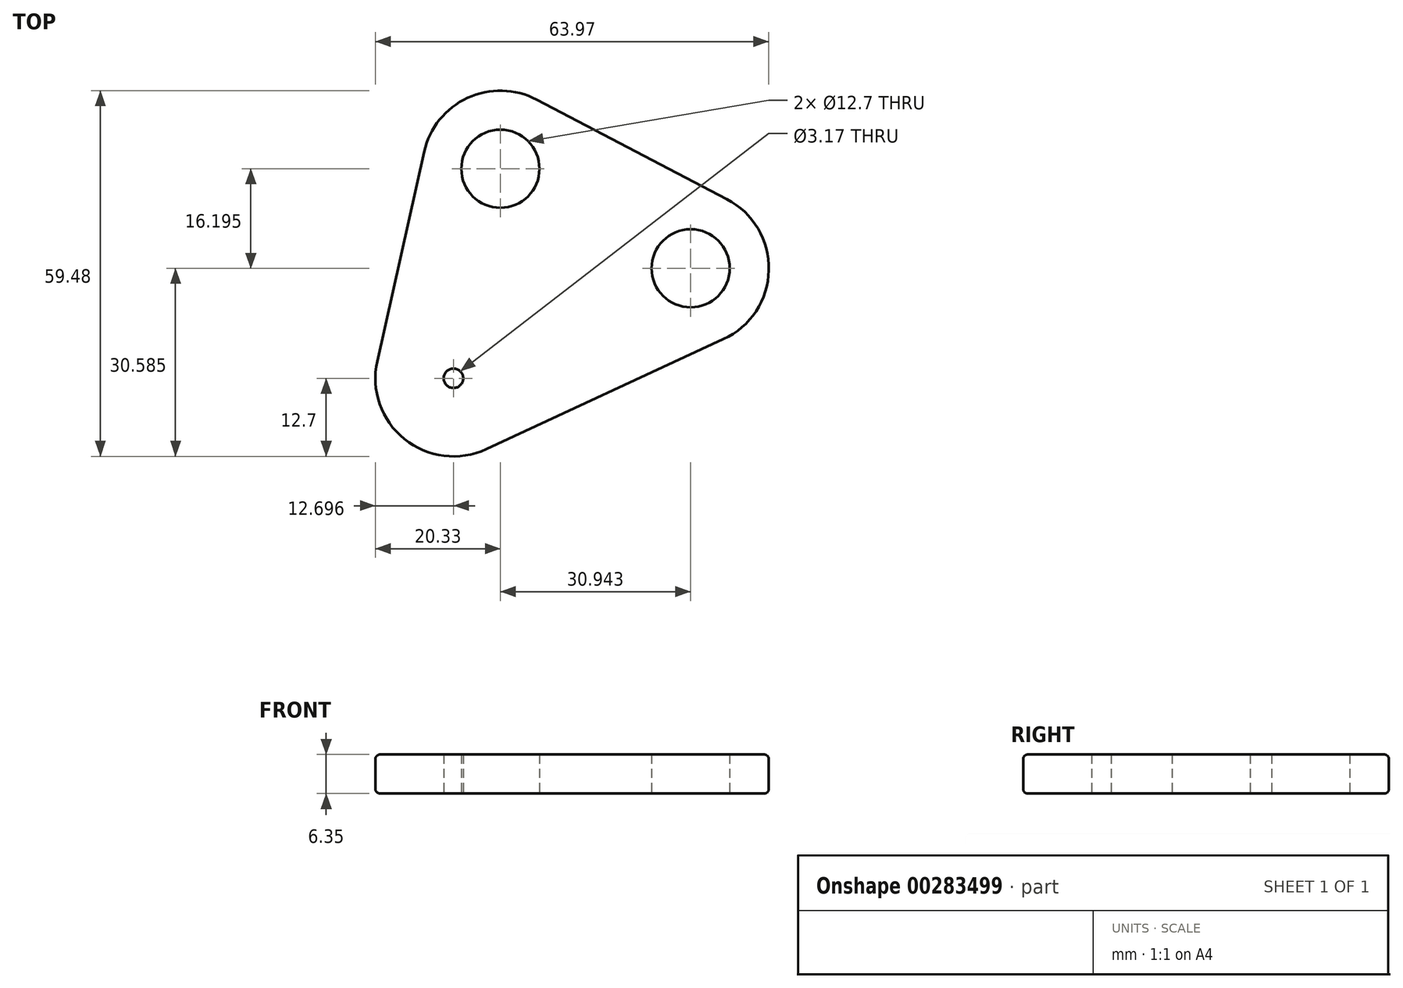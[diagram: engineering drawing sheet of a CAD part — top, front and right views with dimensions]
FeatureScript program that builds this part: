
annotation { "Feature Type Name" : "Feature", "Feature Type Description" : "" }
export const myFeature = defineFeature(function(context is Context, id is Id, definition is map)
    precondition{}
    {
        {
            var Q0;
            Q0=qCreatedBy(makeId("Top.planeOp"),FACE);
            var sketch = newSketch(context, id + "F0", { "sketchPlane" : qUnion([Q0])});
            skCircle(sketch, "E0", {"center": v(0, 0) * mm, "radius": 41.28 * mm, "construction": true});
            skCircle(sketch, "E1.0", {"center": v(0, 0) * mm, "radius": 34.93 * mm, "construction": true});
            skLineSegment(sketch, "E2", {"start": v(-7.63, -34.08) * mm, "end": v(0, 0) * mm, "construction": true});
            skLineSegment(sketch, "E3", {"start": v(0, 0) * mm, "end": v(30.94, -16.2) * mm, "construction": true});
            skLineSegment(sketch, "E4", {"start": v(40.64, 50.8) * mm, "end": v(-86.34, 52.78) * mm});
            skLineSegment(sketch, "E5", {"start": v(30.94, -16.2) * mm, "end": v(39.13, -133.7) * mm});
            skCircle(sketch, "E6", {"center": v(40.64, 50.8) * mm, "radius": 101.6 * mm, "construction": true});
            skLineSegment(sketch, "E7", {"start": v(-60.95, 52.39) * mm, "end": v(-60.95, 52.39) * mm});
            skLineSegment(sketch, "E8", {"start": v(-10.35, 38.9) * mm, "end": v(-7.63, -34.08) * mm, "construction": true});
            skCircle(sketch, "E9.0", {"center": v(0, 0) * mm, "radius": 28.57 * mm, "construction": true});
            skCircle(sketch, "E10.0", {"center": v(40.64, 50.8) * mm, "radius": 100.93 * mm});
            skLineSegment(sketch, "E11.0", {"start": v(5.89, 11.25) * mm, "end": v(36.83, -4.94) * mm});
            skLineSegment(sketch, "E12.0", {"start": v(-20.03, -31.3) * mm, "end": v(-12.4, 2.78) * mm});
            skLineSegment(sketch, "E13", {"start": v(-7.63, -34.08) * mm, "end": v(30.94, -16.2) * mm, "construction": true});
            skLineSegment(sketch, "E14.0", {"start": v(-2.3, -45.6) * mm, "end": v(36.28, -27.72) * mm});
            skArc(sketch, "E15.filletArc", {"start": v(-20.03, -31.3) * mm, "mid": v(-15.6, -43.97) * mm, "end": v(-2.3, -45.6) * mm});
            skArc(sketch, "E16.filletArc", {"start": v(36.28, -27.72) * mm, "mid": v(43.64, -16.5) * mm, "end": v(36.83, -4.94) * mm});
            skArc(sketch, "E17.filletArc", {"start": v(5.89, 11.25) * mm, "mid": v(-5.34, 11.52) * mm, "end": v(-12.4, 2.78) * mm});
            skCircle(sketch, "E18", {"center": v(0, 0) * mm, "radius": 6.35 * mm});
            skCircle(sketch, "E19", {"center": v(-7.63, -34.08) * mm, "radius": 3.18 * mm});
            skCircle(sketch, "E20", {"center": v(30.94, -16.2) * mm, "radius": 6.35 * mm});
            skLineSegment(sketch, "E21", {"start": v(-10.15, 51.6) * mm, "end": v(-10.35, 38.9) * mm});
            skCircle(sketch, "E22", {"center": v(-10.35, 38.9) * mm, "radius": 3.18 * mm});
            skArc(sketch, "E23", {"start": v(-10.35, 38.9) * mm, "mid": v(-18.3, 2.06) * mm, "end": v(-7.63, -34.08) * mm, "construction": true});
            skArc(sketch, "E24.0", {"start": v(-4.67, 36.06) * mm, "mid": v(-7.52, 44.58) * mm, "end": v(-16.03, 41.73) * mm});
            skArc(sketch, "E25.0", {"start": v(-16.03, 41.73) * mm, "mid": v(-24.65, 1.82) * mm, "end": v(-13.1, -37.33) * mm});
            skArc(sketch, "E26.0", {"start": v(-4.67, 36.06) * mm, "mid": v(-11.96, 2.3) * mm, "end": v(-2.18, -30.83) * mm});
            skArc(sketch, "E27.0", {"start": v(-13.1, -37.33) * mm, "mid": v(-4.39, -39.54) * mm, "end": v(-2.18, -30.83) * mm});
            skSolve(sketch);
        }
        {
            var Q0;
            {var subQ0=sQuery(id+"F0.wireOp",EDGE,"E15.filletArc");Q0=makeQuery(id+"F0.imprint","IMPRINT",FACE,{"disambiguationData":[TD([[makeQuery(id+"F0.imprint","IMPRINT",EDGE,{"derivedFrom":subQ0}),1.0]])]});}
            var Q1;
            {var subQ5=sQuery(id+"F0.wireOp",EDGE,"E11.0");Q1=makeQuery(id+"F0.imprint","IMPRINT",FACE,{"disambiguationData":[TD([[makeQuery(id+"F0.imprint","IMPRINT",EDGE,{"derivedFrom":subQ5}),-1.0]])]});}
            var Q2;
            Q2=makeQuery(id+"F0.imprint","IMPRINT",FACE,{"disambiguationData":[TD([[makeQuery(id+"F0.imprint","IMPRINT",EDGE,{"derivedFrom":sQuery(id+"F0.wireOp",EDGE,"E19")}),-1.0]])]});
            var Q3;
            {var subQ0=sQuery(id+"F0.wireOp",EDGE,"E12.0");var subQ1=sQuery(id+"F0.wireOp",EDGE,"E10.0");var subQ2=makeQuery(id+"F0.imprint","INTERSECT",VERTEX,{"derivedFrom":[subQ1,subQ0]});Q3=makeQuery(id+"F0.imprint","IMPRINT",FACE,{"disambiguationData":[TD([[makeQuery(id+"F0.imprint","IMPRINT",EDGE,{"disambiguationData":[TD([[subQ2,-1.0]])],"derivedFrom":subQ1}),1.0]])]});}
            var Q4;
            {var subQ0=sQuery(id+"F0.wireOp",EDGE,"E25.0");var subQ1=sQuery(id+"F0.wireOp",EDGE,"E10.0");var subQ2=makeQuery(id+"F0.imprint","INTERSECT",VERTEX,{"derivedFrom":[subQ1,subQ0]});Q4=makeQuery(id+"F0.imprint","IMPRINT",FACE,{"disambiguationData":[TD([[makeQuery(id+"F0.imprint","IMPRINT",EDGE,{"disambiguationData":[TD([[subQ2,-1.0]])],"derivedFrom":subQ1}),-1.0]])]});}
            var Q5;
            Q5=makeQuery(id+"F0.imprint","IMPRINT",FACE,{"disambiguationData":[TD([[makeQuery(id+"F0.imprint","IMPRINT",EDGE,{"derivedFrom":sQuery(id+"F0.wireOp",EDGE,"E19")}),1.0]])]});
            extrude(context, id + "F1", {"entities" : qUnion([Q0, Q1, Q2, Q3, Q4, Q5]), "depth" : 6.35 * mm});
        }
        {
            var Q0;
            Q0=makeQuery(id+"F1.opExtrude","CAP_EDGE",EDGE,{"disambiguationData":[OSD([sQuery(id+"F0.wireOp",EDGE,"E15.filletArc")])],"isStart":false});
            var Q1;
            Q1=makeQuery(id+"F1.opExtrude","CAP_EDGE",EDGE,{"disambiguationData":[OSD([sQuery(id+"F0.wireOp",EDGE,"E14.0")])],"isStart":false});
            var Q2;
            Q2=makeQuery(id+"F1.opExtrude","CAP_EDGE",EDGE,{"disambiguationData":[OSD([sQuery(id+"F0.wireOp",EDGE,"E14.0")])],"isStart":true});
            var Q3;
            Q3=makeQuery(id+"F1.opExtrude","CAP_EDGE",EDGE,{"disambiguationData":[OSD([sQuery(id+"F0.wireOp",EDGE,"E15.filletArc")])],"isStart":true});
            fillet(context, id + "F2", {"entities" : qUnion([Q0, Q1, Q2, Q3]), "radius" : 0.76 * mm, "tangentPropagation" : true, "allowEdgeOverflow" : false});
        }
        {
            var Q0;
            Q0=makeQuery(id+"F1.opExtrude","CAP_FACE",FACE,{"disambiguationData":[OSD([sQuery(id+"F0.wireOp",EDGE,"E11.0"),sQuery(id+"F0.wireOp",EDGE,"E12.0"),sQuery(id+"F0.wireOp",EDGE,"E14.0"),sQuery(id+"F0.wireOp",EDGE,"E15.filletArc"),sQuery(id+"F0.wireOp",EDGE,"E16.filletArc"),sQuery(id+"F0.wireOp",EDGE,"E17.filletArc"),sQuery(id+"F0.wireOp",EDGE,"E18"),sQuery(id+"F0.wireOp",EDGE,"E20")])],"isStart":false});
            var sketch = newSketch(context, id + "F3", { "sketchPlane" : qUnion([Q0])});
            skPoint(sketch, "E28.0", {"position": v(-7.63, -34.08) * mm});
            skSolve(sketch);
        }
        {
            var Q0;
            Q0=sQuery(id+"F3.wireOp",VERTEX,"E28.0");
            var Q1;
            Q1=makeQuery(id+"F1.opExtrude","SWEPT_BODY",BODY,{"disambiguationData":[OSD([sQuery(id+"F0.wireOp",EDGE,"E11.0"),sQuery(id+"F0.wireOp",EDGE,"E12.0"),sQuery(id+"F0.wireOp",EDGE,"E14.0"),sQuery(id+"F0.wireOp",EDGE,"E15.filletArc"),sQuery(id+"F0.wireOp",EDGE,"E16.filletArc"),sQuery(id+"F0.wireOp",EDGE,"E17.filletArc"),sQuery(id+"F0.wireOp",EDGE,"E18"),sQuery(id+"F0.wireOp",EDGE,"E20")])]});
            hole(context, id + "F4", {"style" : HoleStyle.SIMPLE, "endStyle" : HoleEndStyle.THROUGH, "holeDiameter" : 3.17 * mm, "tappedDepth" : 12.7 * mm, "tapClearance" : 3, "locations" : qUnion([Q0]), "scope" : qUnion([Q1])});
        }
    });
